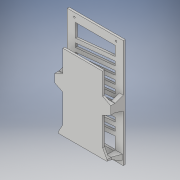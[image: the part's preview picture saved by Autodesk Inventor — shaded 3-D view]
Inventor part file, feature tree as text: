
AUTODESK INVENTOR PART (.ipt)
format: ipt  version: 2018 (Build 220112000, 112)  size: 413,696 bytes
history: native  units: in
note: dims shown in document units (in); Inventor stores cm internally (conversion verified against a paired STEP export)
features: sketch x11, extrude x9, chamfer x9, projected_geometry x6, plane x2, mirror x1
ambient origin geometry x8: Origin, YZ Plane, XZ Plane, XY Plane, X Axis, Y Axis, Z Axis, Center Point
bodies: Solid1 (feature_tree)
feature tree (38):
  extrude  "Extrusion1"  Depth=3.46in
  sketch  "Sketch2"  dims[d2=0.1in d3=0.1in]
  sketch  "Sketch4"  dims[d4=0.1in d5=0.1in]
  extrude  "Extrusion2"  Depth=0.1in
  extrude  "Extrusion3"  Depth=0.1in
  extrude  "Extrusion4"  Depth=0.25in
  plane  "Work Plane1"
  mirror  "Mirror1"
  chamfer  "Chamfer2"  Distance=0.125in
  chamfer  "Chamfer3"  Distance=2.208in
  chamfer  "Chamfer4"  Distance=0.105in
  chamfer  "Chamfer5"  Distance=0.105in
  chamfer  "Chamfer6"  Distance=0.105in
  chamfer  "Chamfer7"  Distance=0.105in
  extrude  "Extrusion5"  Depth=0.125in
  plane  "Work Plane2"
  extrude  "Extrusion7"  Depth=0.125in
  extrude  "Extrusion8"  Depth=0.125in
  chamfer  "Chamfer8"  Distance=0.136in
  extrude  "Extrusion9"  Depth=0.125in
  chamfer  "Chamfer9"  Distance=0.136in
  chamfer  "Chamfer10"  Distance=0.136in
  extrude  "Extrusion10"  Depth=0.125in
  sketch  "Sketch1"  dims[d0=6.6875in d1=3.46in]
  projected_geometry  "Projected Loop2"
  sketch  "Sketch5"  dims[d6=0.44in d7=0.25in]
  projected_geometry  "Projected Loop3"
  sketch  "Sketch6"  dims[d8=0.25in]
  sketch  "Sketch7"  dims[d9=0.44in]
  sketch  "Sketch8"  dims[d10=0.44in]
  sketch  "Sketch10"  dims[d11=0.44in]
  sketch  "Sketch11"  dims[d12=0.25in]
  projected_geometry  "Projected Loop4"
  projected_geometry  "Projected Loop5"
  projected_geometry  "Projected Loop6"
  projected_geometry  "Projected Loop7"
  sketch  "Sketch12"  dims[d13=0.25in d14=0.125in d15=0.0in]
  sketch  "Sketch13"  dims[d16=3.345in d17=2.208in d18=0.105in d19=0.105in d20=0.105in d21=0.105in d22=0.927in d23=0.927in d24=0.136in d25=0.136in d26=0.136in d27=0.136in d28=0.136in d29=0.136in d30=0.626in d31=0.626in d48=0.5in d49=4.5in d50=0.594in d51=0.25in d52=0.25in d53=0.25in d54=0.25in d55=0.25in d56=0.25in d57=0.25in d58=0.25in d59=0.25in d60=0.25in d61=0.25in d64=0.25in d65=0.25in d66=0.25in d67=0.25in d68=0.25in d69=0.25in d70=0.25in d73=0.125in d74=0.0in d75=0.25in d76=0.25in d77=0.25in d78=0.25in d79=0.125in d80=0.0in d81=3.0in d82=0.23in d83=5.5in d84=0.594in d85=0.0in d86=0.0in d89=0.25in d90=0.5in d91=0.5in d92=0.0in d96=0.5in d97=0.125in d98=0.1374in d99=0.5in d100=0.125in d101=0.1374in d102=0.5in d103=0.125in d104=0.1374in d105=0.5in d106=0.125in d107=0.1374in d108=0.5in d109=0.125in d110=0.1374in d111=0.5in d112=0.125in d113=0.1374in d115=0.25in d116=0.25in d117=2.0in d118=0.0in d119=0.65in d122=0.125in d123=0.0in d124=0.125in d125=0.0in d126=0.125in d127=0.125in d128=45.0deg d129=1.0in d130=0.125in d131=0.0in d132=0.65in d133=0.125in d134=0.1374in d135=0.65in d136=0.125in d137=0.1374in d138=0.25in d139=0.25in d140=2.0in d141=0.0in]
